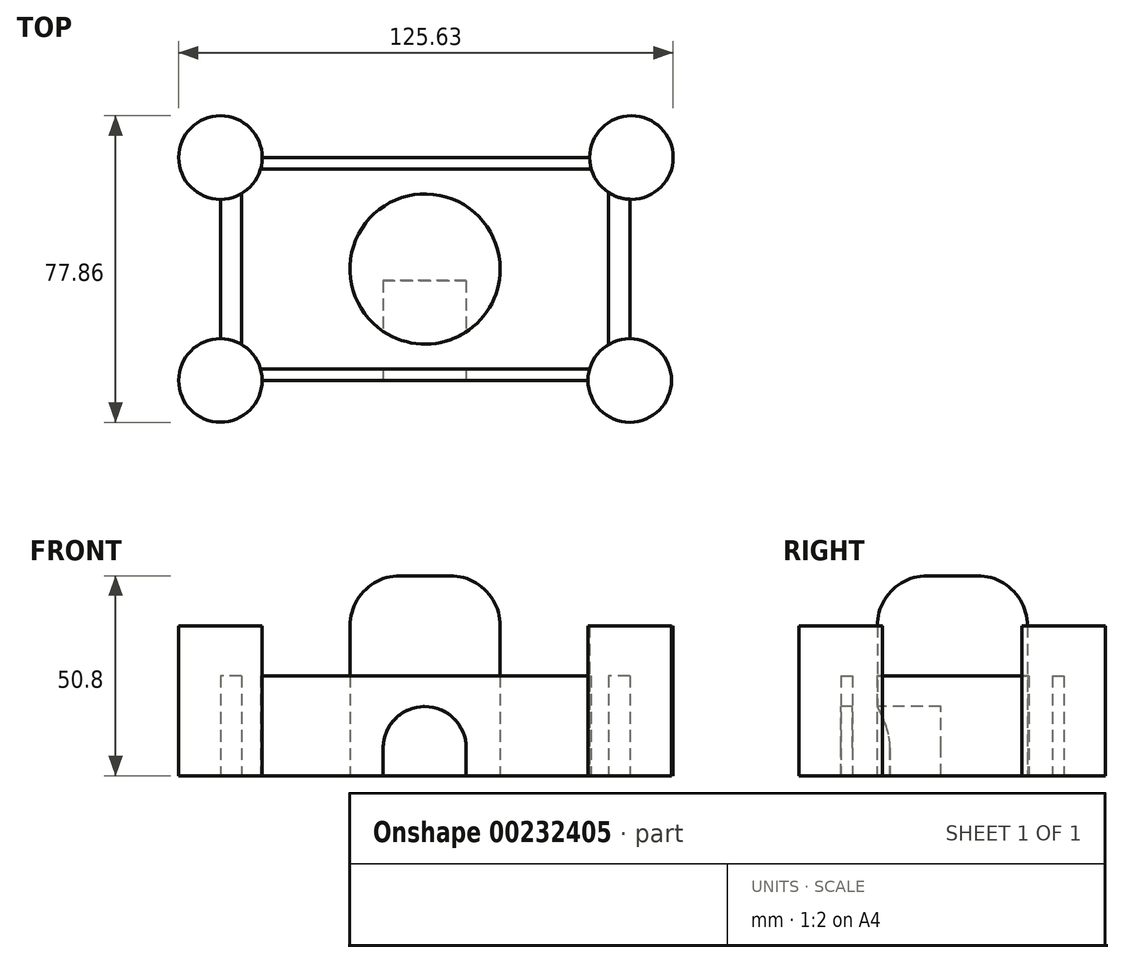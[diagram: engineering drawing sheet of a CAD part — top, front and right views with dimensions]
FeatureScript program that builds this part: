
annotation { "Feature Type Name" : "Feature", "Feature Type Description" : "" }
export const myFeature = defineFeature(function(context is Context, id is Id, definition is map)
    precondition{}
    {
        {
            var Q0;
            Q0=qCreatedBy(makeId("Top.planeOp"),FACE);
            var sketch = newSketch(context, id + "F0", { "sketchPlane" : qUnion([Q0])});
            skLineSegment(sketch, "E0.bottom", {"start": v(-41.4, -28.32) * mm, "end": v(41.38, -28.32) * mm});
            skLineSegment(sketch, "E0.top", {"start": v(-41.39, 28.32) * mm, "end": v(41.8, 28.32) * mm});
            skLineSegment(sketch, "E0.left", {"start": v(-52, -17.69) * mm, "end": v(-52, 17.72) * mm});
            skLineSegment(sketch, "E0.right", {"start": v(52, -17.71) * mm, "end": v(52, 17.72) * mm});
            skPoint(sketch, "E0.middle", {"position": v(0, 0) * mm});
            skCircle(sketch, "E1", {"center": v(0, 0) * mm, "radius": 19.08 * mm});
            skCircle(sketch, "E2", {"center": v(-52, 28.32) * mm, "radius": 10.6 * mm});
            skCircle(sketch, "E3", {"center": v(52.4, 28.32) * mm, "radius": 10.6 * mm});
            skCircle(sketch, "E4", {"center": v(52, -28.32) * mm, "radius": 10.6 * mm});
            skCircle(sketch, "E5", {"center": v(-52, -28.3) * mm, "radius": 10.6 * mm});
            skLineSegment(sketch, "E6.bottom", {"start": v(-41.8, -25.43) * mm, "end": v(41.78, -25.43) * mm});
            skLineSegment(sketch, "E6.top", {"start": v(-41.8, 25.43) * mm, "end": v(42.2, 25.43) * mm});
            skLineSegment(sketch, "E6.left", {"start": v(-46.62, -19.16) * mm, "end": v(-46.62, 19.18) * mm});
            skLineSegment(sketch, "E6.right", {"start": v(46.62, -19.17) * mm, "end": v(46.62, 19.43) * mm});
            skPoint(sketch, "E7.orphan", {"position": v(52, 28.32) * mm});
            skPoint(sketch, "E8.orphan", {"position": v(-52, -28.32) * mm});
            skPoint(sketch, "E9.orphan", {"position": v(46.62, -25.43) * mm});
            skPoint(sketch, "E10.orphan", {"position": v(46.62, 25.43) * mm});
            skPoint(sketch, "E11.orphan", {"position": v(-46.62, 25.43) * mm});
            skPoint(sketch, "E12.orphan", {"position": v(-46.62, -25.43) * mm});
            skSolve(sketch);
        }
        {
            var Q0;
            {var subQ0=sQuery(id+"F0.wireOp",EDGE,"E0.top");Q0=makeQuery(id+"F0.imprint","IMPRINT",FACE,{"disambiguationData":[TD([[makeQuery(id+"F0.imprint","IMPRINT",EDGE,{"derivedFrom":subQ0}),-1.0]])]});}
            var Q1;
            {var subQ0=sQuery(id+"F0.wireOp",EDGE,"E0.left");Q1=makeQuery(id+"F0.imprint","IMPRINT",FACE,{"disambiguationData":[TD([[makeQuery(id+"F0.imprint","IMPRINT",EDGE,{"derivedFrom":subQ0}),-1.0]])]});}
            var Q2;
            {var subQ0=sQuery(id+"F0.wireOp",EDGE,"E0.bottom");Q2=makeQuery(id+"F0.imprint","IMPRINT",FACE,{"disambiguationData":[TD([[makeQuery(id+"F0.imprint","IMPRINT",EDGE,{"derivedFrom":subQ0}),1.0]])]});}
            var Q3;
            {var subQ0=sQuery(id+"F0.wireOp",EDGE,"E0.right");Q3=makeQuery(id+"F0.imprint","IMPRINT",FACE,{"disambiguationData":[TD([[makeQuery(id+"F0.imprint","IMPRINT",EDGE,{"derivedFrom":subQ0}),1.0]])]});}
            extrude(context, id + "F1", {"entities" : qUnion([Q0, Q1, Q2, Q3]), "depth" : 25.4 * mm});
        }
        {
            var Q0;
            {var subQ0=sQuery(id+"F0.wireOp",EDGE,"E2");var subQ1=makeQuery(id+"F0.imprint","INTERSECT",VERTEX,{"derivedFrom":[sQuery(id+"F0.wireOp",EDGE,"E0.top"),subQ0]});Q0=makeQuery(id+"F0.imprint","IMPRINT",FACE,{"disambiguationData":[TD([[makeQuery(id+"F0.imprint","IMPRINT",EDGE,{"disambiguationData":[TD([[subQ1,-1.0]])],"derivedFrom":subQ0}),1.0]])]});}
            var Q1;
            {var subQ0=sQuery(id+"F0.wireOp",EDGE,"E5");var subQ1=makeQuery(id+"F0.imprint","INTERSECT",VERTEX,{"derivedFrom":[subQ0,sQuery(id+"F0.wireOp",EDGE,"E6.bottom")]});Q1=makeQuery(id+"F0.imprint","IMPRINT",FACE,{"disambiguationData":[TD([[makeQuery(id+"F0.imprint","IMPRINT",EDGE,{"disambiguationData":[TD([[subQ1,-1.0]])],"derivedFrom":subQ0}),1.0]])]});}
            var Q2;
            {var subQ0=sQuery(id+"F0.wireOp",EDGE,"E4");var subQ1=makeQuery(id+"F0.imprint","INTERSECT",VERTEX,{"derivedFrom":[sQuery(id+"F0.wireOp",EDGE,"E0.right"),subQ0]});Q2=makeQuery(id+"F0.imprint","IMPRINT",FACE,{"disambiguationData":[TD([[makeQuery(id+"F0.imprint","IMPRINT",EDGE,{"disambiguationData":[TD([[subQ1,-1.0]])],"derivedFrom":subQ0}),1.0]])]});}
            var Q3;
            {var subQ0=sQuery(id+"F0.wireOp",EDGE,"E3");var subQ1=makeQuery(id+"F0.imprint","INTERSECT",VERTEX,{"derivedFrom":[sQuery(id+"F0.wireOp",EDGE,"E0.top"),subQ0]});Q3=makeQuery(id+"F0.imprint","IMPRINT",FACE,{"disambiguationData":[TD([[makeQuery(id+"F0.imprint","IMPRINT",EDGE,{"disambiguationData":[TD([[subQ1,-1.0]])],"derivedFrom":subQ0}),1.0]])]});}
            extrude(context, id + "F2", {"entities" : qUnion([Q0, Q1, Q2, Q3]), "depth" : 38.1 * mm});
        }
        {
            var Q0;
            Q0=makeQuery(id+"F0.imprint","IMPRINT",FACE,{"disambiguationData":[TD([[makeQuery(id+"F0.imprint","IMPRINT",EDGE,{"derivedFrom":sQuery(id+"F0.wireOp",EDGE,"E1")}),1.0]])]});
            extrude(context, id + "F3", {"entities" : qUnion([Q0]), "depth" : 50.8 * mm});
        }
        {
            var Q0;
            Q0=makeQuery(id+"F1.opExtrude","SWEPT_FACE",FACE,{"disambiguationData":[OSD([sQuery(id+"F0.wireOp",EDGE,"E0.bottom")])]});
            var sketch = newSketch(context, id + "F4", { "sketchPlane" : qUnion([Q0])});
            skLineSegment(sketch, "E13.bottom", {"start": v(-10.65, 0) * mm, "end": v(10.44, 0) * mm});
            skLineSegment(sketch, "E13.left", {"start": v(-10.65, 0) * mm, "end": v(-10.65, 7.03) * mm});
            skLineSegment(sketch, "E13.right", {"start": v(10.44, 0) * mm, "end": v(10.44, 7.03) * mm});
            skArc(sketch, "E14", {"start": v(10.44, 7.03) * mm, "mid": v(-0.1, 17.57) * mm, "end": v(-10.65, 7.03) * mm});
            skSolve(sketch);
        }
        {
            var Q0;
            Q0=makeQuery(id+"F4.imprint","IMPRINT",FACE,{"disambiguationData":[TD([[makeQuery(id+"F4.imprint","IMPRINT",EDGE,{"derivedFrom":sQuery(id+"F4.wireOp",EDGE,"E13.bottom")}),1.0]])]});
            extrude(context, id + "F5", {"entities" : qUnion([Q0]), "operationType" : NewBodyOperationType.REMOVE, "oppositeDirection" : true, "depth" : 25.4 * mm});
        }
        {
            var Q0;
            Q0=makeQuery(id+"F3.opExtrude","CAP_FACE",FACE,{"disambiguationData":[OSD([sQuery(id+"F0.wireOp",EDGE,"E1")])],"isStart":false});
            fillet(context, id + "F6", {"entities" : qUnion([Q0]), "radius" : 12.7 * mm, "tangentPropagation" : true, "allowEdgeOverflow" : false});
        }
    });
